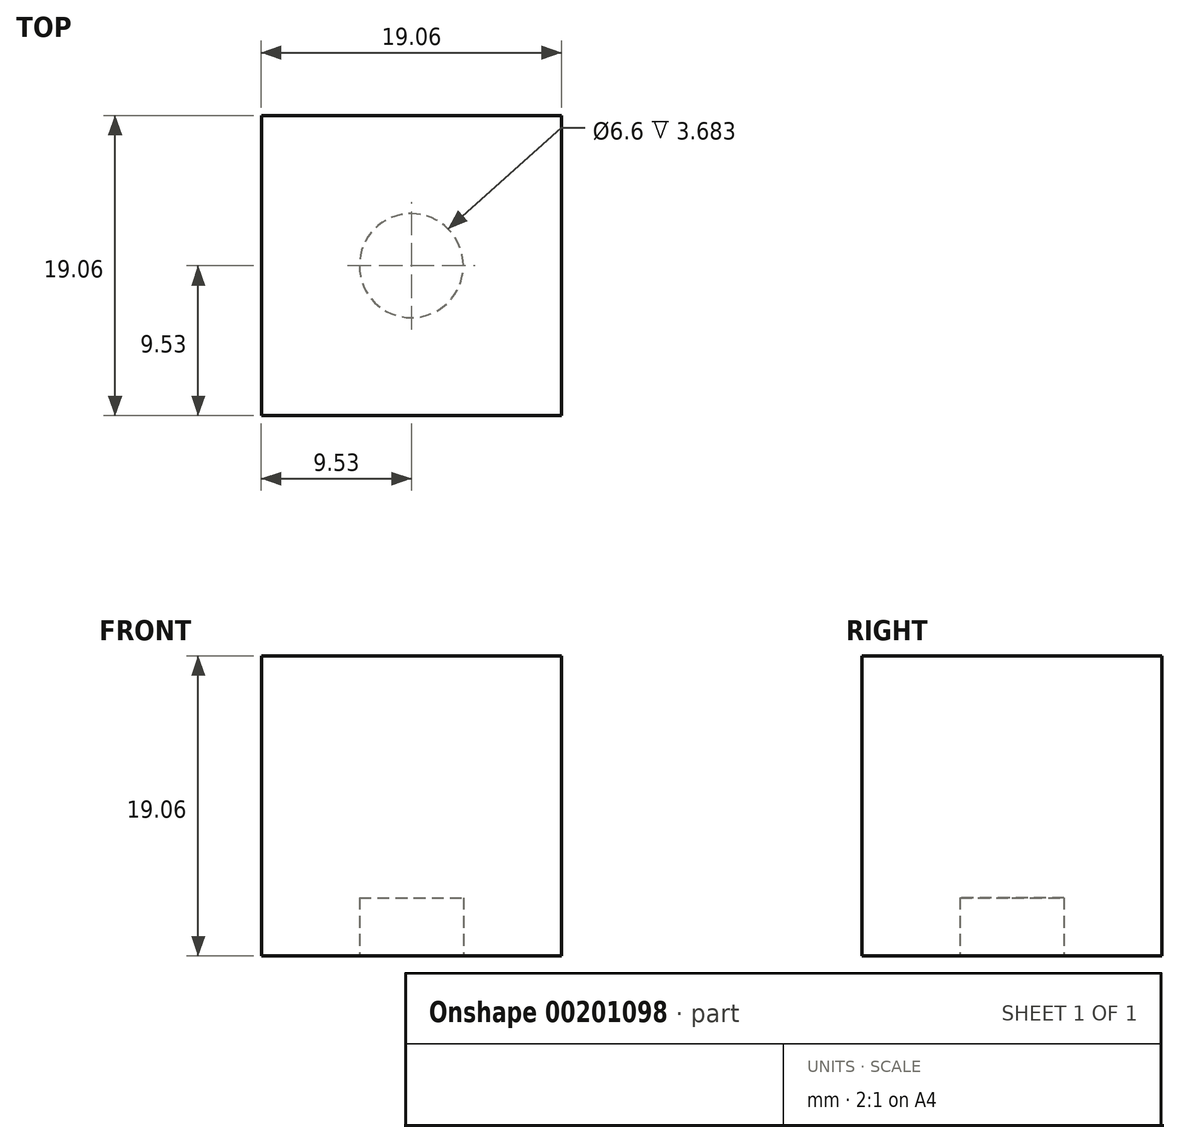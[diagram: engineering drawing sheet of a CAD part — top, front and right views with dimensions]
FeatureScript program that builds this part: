
annotation { "Feature Type Name" : "Feature", "Feature Type Description" : "" }
export const myFeature = defineFeature(function(context is Context, id is Id, definition is map)
    precondition{}
    {
        {
            var Q0;
            Q0=qCreatedBy(makeId("Top.planeOp"),FACE);
            var sketch = newSketch(context, id + "F0", { "sketchPlane" : qUnion([Q0])});
            skLineSegment(sketch, "E0.bottom", {"start": v(-9.52, 9.53) * mm, "end": v(9.52, 9.53) * mm});
            skLineSegment(sketch, "E0.top", {"start": v(-9.52, -9.53) * mm, "end": v(9.52, -9.53) * mm});
            skLineSegment(sketch, "E0.left", {"start": v(-9.53, 9.52) * mm, "end": v(-9.53, -9.52) * mm});
            skLineSegment(sketch, "E0.right", {"start": v(9.53, 9.52) * mm, "end": v(9.53, -9.52) * mm});
            skSolve(sketch);
        }
        {
            var Q0;
            Q0=qSketchRegion(id+"F0",true);
            extrude(context, id + "F1", {"entities" : qUnion([Q0]), "endBound" : BoundingType.SYMMETRIC, "depth" : 19.05 * mm});
        }
        {
            var Q0;
            Q0=makeQuery(id+"F1.opExtrude","CAP_FACE",FACE,{"disambiguationData":[OSD([sQuery(id+"F0.wireOp",EDGE,"E0.bottom"),sQuery(id+"F0.wireOp",EDGE,"E0.top"),sQuery(id+"F0.wireOp",EDGE,"E0.left"),sQuery(id+"F0.wireOp",EDGE,"E0.right")])],"isStart":true});
            var sketch = newSketch(context, id + "F2", { "sketchPlane" : qUnion([Q0])});
            skCircle(sketch, "E1", {"center": v(0, 0) * mm, "radius": 3.3 * mm});
            skSolve(sketch);
        }
        {
            var Q0;
            Q0=qSketchRegion(id+"F2",true);
            extrude(context, id + "F3", {"entities" : qUnion([Q0]), "operationType" : NewBodyOperationType.REMOVE, "oppositeDirection" : true, "depth" : 3.68 * mm});
        }
    });
